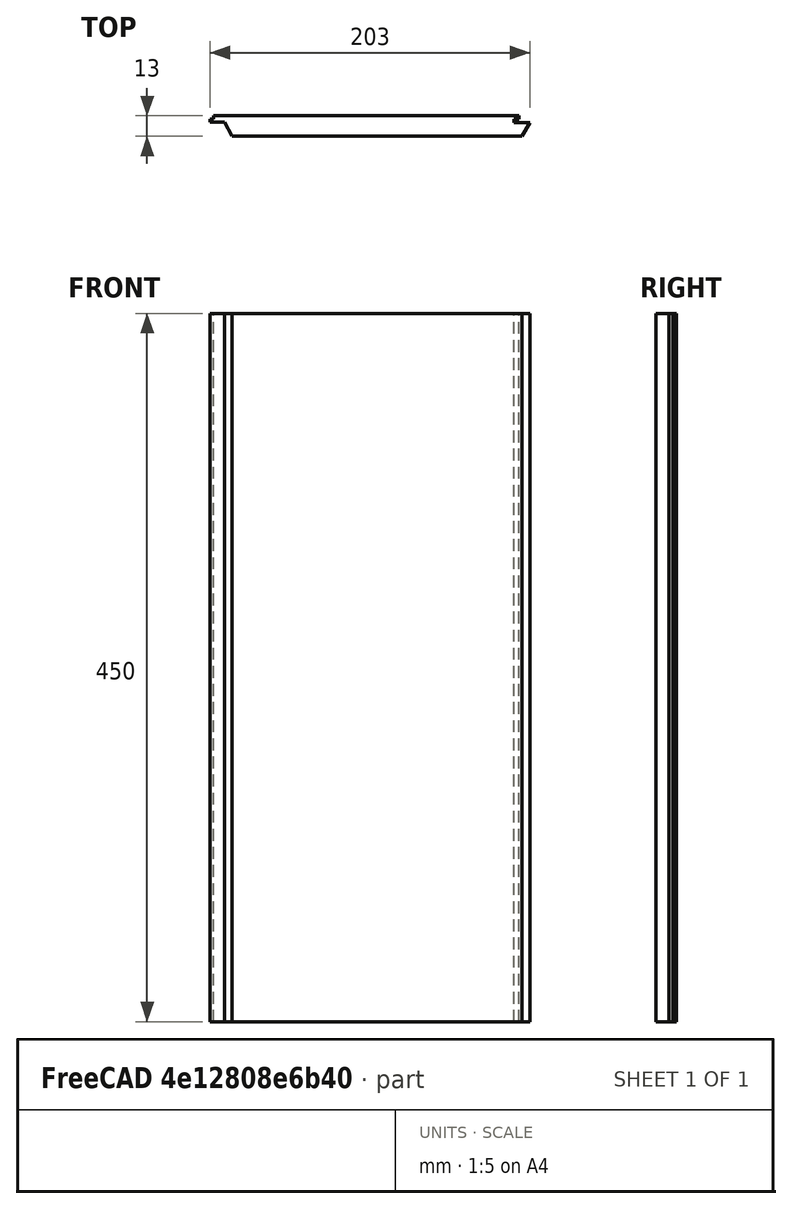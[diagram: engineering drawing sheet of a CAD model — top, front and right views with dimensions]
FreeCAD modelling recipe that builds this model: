
FCSTD DOCUMENT  (FreeCAD 0.19R24276 (Git))
Label: Parket_L450
License: All rights reserved
LicenseURL: http://en.wikipedia.org/wiki/All_rights_reserved
objects: Sketcher::SketchObject×1, PartDesign::Pad×1, PartDesign::Body×1
note: 4 computed .brp shape members not serialized (recipe doc carries the construction recipe); baked Part::Feature solids carry a one-line shape summary decoded from their .brp

FEATURE [Sketcher::SketchObject] Sketch
  FullyConstrained = true
  MapMode = 5
  Support = -> [XY_Plane]
  sketch-geometry (14):
    g0: LineSegment StartX=0 StartY=0 StartZ=0 EndX=184 EndY=0 EndZ=0
    g1: LineSegment StartX=184 StartY=0 StartZ=0 EndX=184 EndY=8.5 EndZ=0
    g2: LineSegment StartX=184 StartY=0 StartZ=0 EndX=189 EndY=8.5 EndZ=0
    g3: LineSegment StartX=184 StartY=8.5 StartZ=0 EndX=179 EndY=8.5 EndZ=0
    g4: LineSegment StartX=179 StartY=8.5 StartZ=0 EndX=179 EndY=11 EndZ=0
    g5: LineSegment StartX=179 StartY=11 StartZ=0 EndX=182 EndY=11 EndZ=0
    g6: LineSegment StartX=182 StartY=11 StartZ=0 EndX=182 EndY=13 EndZ=0
    g7: LineSegment StartX=182 StartY=13 StartZ=0 EndX=-12 EndY=13 EndZ=0
    g8: LineSegment StartX=184 StartY=8.5 StartZ=0 EndX=189 EndY=8.5 EndZ=0
    g9: LineSegment StartX=-12 StartY=13 StartZ=0 EndX=-12 EndY=11 EndZ=0
    g10: LineSegment StartX=-12 StartY=11 StartZ=0 EndX=-14 EndY=11 EndZ=0
    g11: LineSegment StartX=-14 StartY=11 StartZ=0 EndX=-14 EndY=9 EndZ=0
    g12: LineSegment StartX=-14 StartY=9 StartZ=0 EndX=-5 EndY=9 EndZ=0
    g13: LineSegment StartX=-5 StartY=9 StartZ=0 EndX=0 EndY=0 EndZ=0
  constraints (40):
    c: Coincident(g0,g-1)
    c: PointOnObject(g0,g-1)
    c: DistanceX(g0,g0) = 184
    c: Coincident(g1,g0)
    c: Vertical(g1)
    c: DistanceY(g1,g1) = 8.5
    c: Coincident(g2,g0)
    c: Coincident(g3,g1)
    c: DistanceX(g3,g3) = 5
    c: Horizontal(g3)
    c: Coincident(g4,g3)
    c: Vertical(g4)
    c: DistanceY(g4,g4) = 2.5
    c: Coincident(g5,g4)
    c: Horizontal(g5)
    c: DistanceX(g5,g5) = 3
    c: Coincident(g6,g5)
    c: Vertical(g6)
    c: Coincident(g7,g6)
    c: Horizontal(g7)
    c: Coincident(g8,g1)
    c: Horizontal(g8)
    c: Coincident(g2,g8)
    c: DistanceX(g7,g7) = 194
    c: Coincident(g9,g7)
    c: Vertical(g9)
    c: Coincident(g10,g9)
    c: Coincident(g11,g10)
    c: Coincident(g12,g11)
    c: Horizontal(g12)
    c: Coincident(g13,g12)
    c: Coincident(g13,g-1)
    c: DistanceX(g10,g10) = 2
    c: Vertical(g11)
    c: DistanceY(g9,g9) = 2
    c: Horizontal(g10)
    c: DistanceY(g11,g11) = 2
    c: DistanceY(g6,g6) = 2
    c: DistanceX(g12,g-1) = 5
    c: DistanceX(g0,g2) = 5
FEATURE [PartDesign::Pad] Pad
  Direction = (1,1,1)
  Length = 450
  Length2 = 100
  Profile = -> Sketch
  Type = 0
FEATURE [PartDesign::Body] Body
  Group = -> [Sketch,Pad]
  Origin = -> Origin
  Tip = -> Pad
